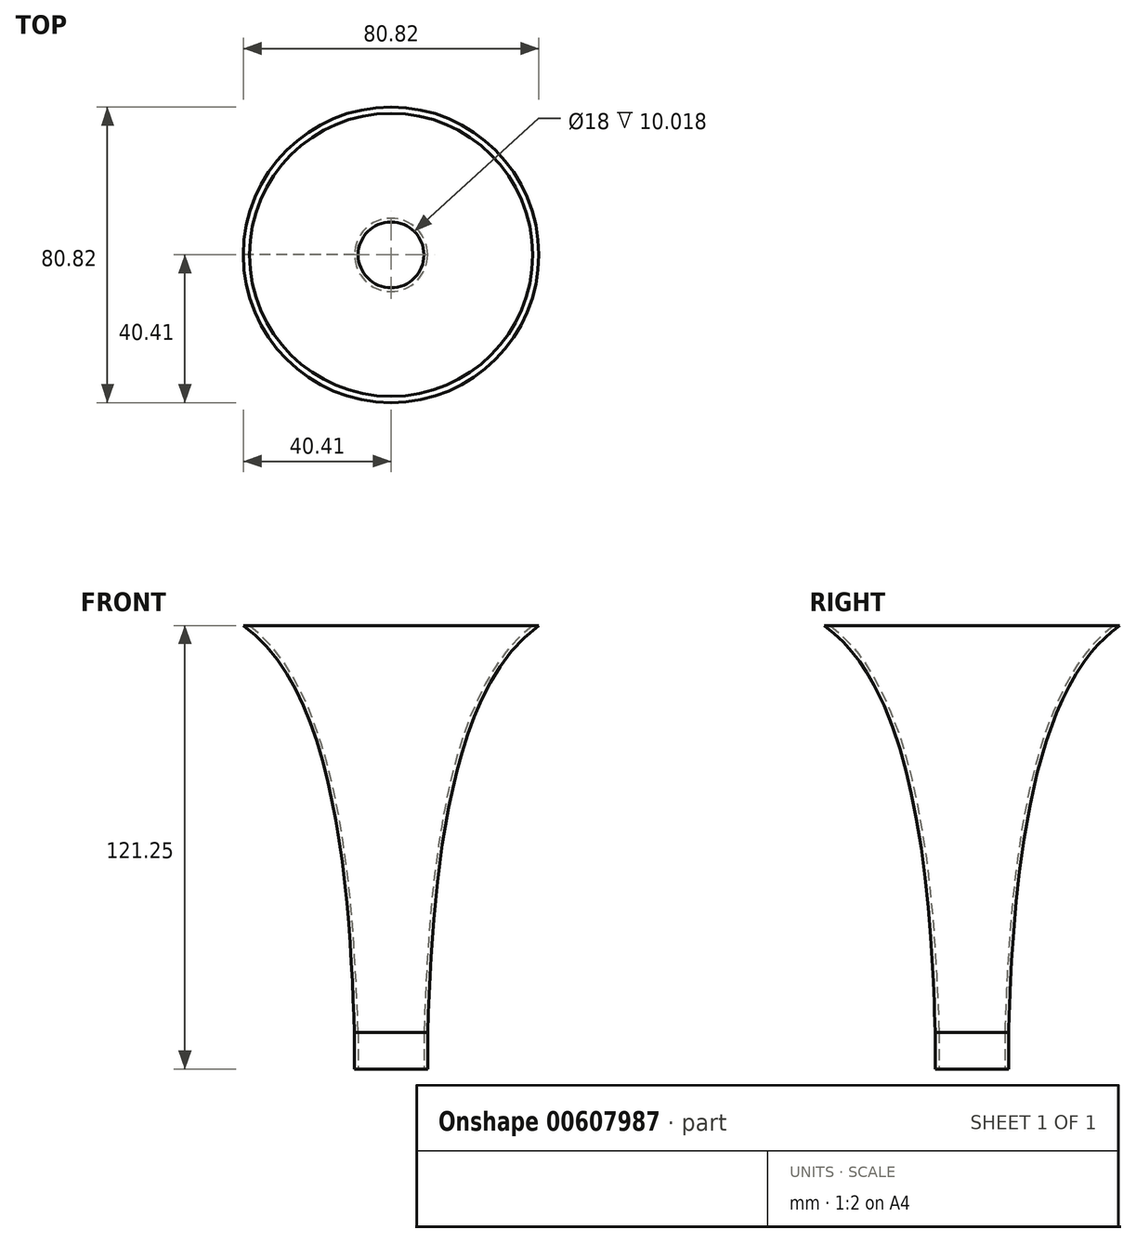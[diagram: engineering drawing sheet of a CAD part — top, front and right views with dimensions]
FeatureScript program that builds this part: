
annotation { "Feature Type Name" : "Feature", "Feature Type Description" : "" }
export const myFeature = defineFeature(function(context is Context, id is Id, definition is map)
    precondition{}
    {
        {
            var Q0;
            Q0=qCreatedBy(makeId("Front.planeOp"),FACE);
            var sketch = newSketch(context, id + "F0", { "sketchPlane" : qUnion([Q0])});
            skLineSegment(sketch, "E0", {"start": v(0, 0) * mm, "end": v(0, 121.25) * mm});
            skLineSegment(sketch, "E1", {"start": v(0, 0) * mm, "end": v(-10, 0) * mm});
            skLineSegment(sketch, "E2", {"start": v(-10, 0) * mm, "end": v(-10, 10) * mm});
            skFitSpline(sketch, "E3", {"points": [v(-10, 10) * mm, v(-40.41, 121.25) * mm], "startDerivative": vector(-3.47, 97.52) * mm, "endDerivative": vector(-80.03, 55.74) * mm});
            skLineSegment(sketch, "E4", {"start": v(-40.41, 121.25) * mm, "end": v(0, 121.25) * mm});
            skSolve(sketch);
        }
        {
            var Q0;
            Q0=makeQuery(id+"F0.imprint","IMPRINT",FACE,{"disambiguationData":[TD([[makeQuery(id+"F0.imprint","IMPRINT",EDGE,{"derivedFrom":sQuery(id+"F0.wireOp",EDGE,"E0")}),1.0]])]});
            var Q1;
            Q1=sQuery(id+"F0.wireOp",EDGE,"E0");
            revolve(context, id + "F1", {"entities" : qUnion([Q0]), "axis" : qUnion([Q1]), "revolveType" : RevolveType.FULL});
        }
        {
            var Q0;
            Q0=makeQuery(id+"F1.opRevolve","SWEPT_FACE",FACE,{"disambiguationData":[OSD([sQuery(id+"F0.wireOp",EDGE,"E1")])]});
            var Q1;
            Q1=makeQuery(id+"F1.opRevolve","SWEPT_FACE",FACE,{"disambiguationData":[OSD([sQuery(id+"F0.wireOp",EDGE,"E4")])]});
            shell(context, id + "F2", {"entities" : qUnion([Q0, Q1]), "thickness" : 1 * mm});
        }
    });
